# Revit family: 63_UN_Road_LumaMiniGen2 _Signify
name_source: partatom
category: Lighting Fixtures
units: mm (PartAtom-declared; Revit-internal decimal feet)

## family parameters
Always vertical = Yes
Cut with Voids When Loaded = Yes
Light Source = Yes
OmniClass Number = 23.80.70.14.21
OmniClass Title = Street and Roadway Lighting
Part Type = Normal
Room Calculation Point = Yes
Round Connector Dimension = Use Diameter
Shared = No
Work Plane-Based = No

## types (5) — shared parameters
Assembly Code = 63.0
Color Filter = 16777215
Description = IP66
Dimming Lamp Color Temperature Shift = <None>
Emit Shape Visible in Rendering = No
Emit from Rectangle Length = 313 mm  [stored 1.0269 ft]
Emit from Rectangle Width = 220 mm  [stored 0.721785 ft]
Housing_Material = Aluminum
IK Value = IK09
IfcExportAs = IfcLightFixtureType
IfcExportType = USERDEFINED
Lamp = LED
Manufacturer = Signify
Model = Luma Mini
Tilt Angle = 90.00°
Type Comments = Gen 2
URL = https://www.signify.com
Voltage = 230 V

## per-type parameters (varying)
| type | Apparent Load | Luminous Flux (lm) | Photometric Web File | Wattage Comments |
| OFMT1_BGP713T251xLED30-4S740DM11 | 19 VA | 3000 lm | OFMT1_BGP713T251xLED30-4S740DM11.IES | 19W |
| OFMT1_BGP713T251xLED100-4S830DW50 | 19 VA | 10000 lm | OFMT1_BGP713T251xLED100-4S830DW50.IES | 18.8W |
| OFMT1_BGP713T251xLED120-4S740DM50 | 73 VA | 12000 lm | OFMT1_BGP713T251xLED120-4S740DM50.IES | 73W |
| OFMT1_BGP7011xLED40-4S740DM10 | 25 VA | 4000 lm | OFMT1_BGP7011xLED40-4S740DM10.IES | 25W |
| OFMT1_BGP7051xLED300-4S740DM11 | 174 VA | 30010 lm | OFMT1_BGP713T251xLED30-4S740DM11.IES | 174W |

note: [stored X ft] marks values corroborated as IEEE doubles in the binary element streams (Revit-internal decimal feet)

## geometry (parser evidence)
native form markers: Sweep x13
no freeform markers — native parametric forms only
